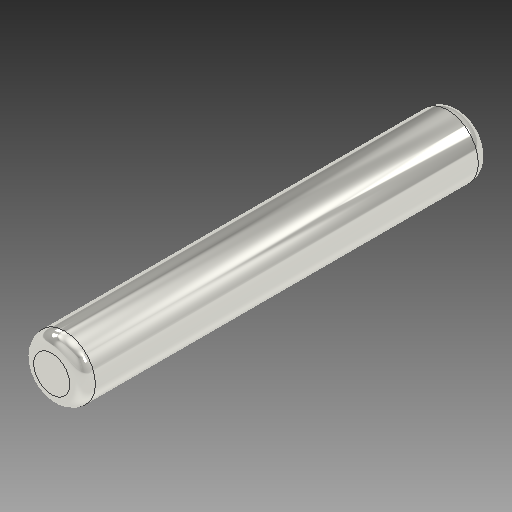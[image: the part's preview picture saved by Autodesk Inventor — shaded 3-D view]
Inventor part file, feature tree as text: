
AUTODESK INVENTOR PART (.ipt)
format: ipt  version: 2021 (Build 250183000, 183)  size: 1,109,504 bytes
history: native  units: mm
features: sketch x2, extrude x1, fillet x1, emboss x1
ambient origin geometry x8: Origin, YZ Plane, XZ Plane, XY Plane, X Axis, Y Axis, Z Axis, Center Point
bodies: Solid1 (feature_tree)
feature tree (5):
  extrude  "Extrusion1"  Depth=5.0mm TaperAngle=0.0deg
  fillet  "Fillet1"  Radius=5.0mm
  emboss  "Emboss1"
  sketch  "Sketch1"  dims[d0=24.181mm d1=160.0mm d2=0.0mm d3=5.0mm]
  sketch  "Sketch2"  dims[d5=15.0mm d6=5.0mm d7=0.0mm]
